# Revit family: Soap_Dispenser-Gamco-Vertical_Tank_Type-G-16AP
name_source: partatom
category: Specialty Equipment
revit_build: Autodesk Revit 2018 (Build: 20170223_1515(x64)
units: mm (PartAtom-declared; Revit-internal decimal feet)

## family parameters
Cut with Voids When Loaded = No
Host = Face
OmniClass Number = 23.40.20.21.34
OmniClass Title = Soap Holders, Dispensers
Part Type = Normal
Room Calculation Point = No
Round Connector Dimension = Use Diameter
Shared = Yes

## types (1)
- G-16AP
    ADA = Yes
    ADA Compliant = Yes
    Assembly Code = C1030200
    Capacity = 40-fl oz. (1.2-L) of liquid lotion soap
    Container Material = Metal-Gamco-Stainless Steel
    Default Elevation = 0"
    Description = Surface-Mounted Vertical Tank-Type Soap Dispenser with All-Purpose Valve
    Height = 8 1/4"
    Installation Type = Wall Mounted
    Length = 4 3/4"
    Manufacturer = GAMCO
    Material = Metal-Gamco-Stainless Steel
    Model = G-16AP
    Mounting Height = 44"
    Price = Prices may vary. Please consult Manufacturer Representative for most up-to-date price list.
    Product Documentation Link = http://gamcousa.com
    Product Page URL = https://gamcousa.com
    Push Button And Spout Material = Plastic-Gamco-Black
    URL = https://gamcousa.com
    Warranty Documentation Link = http://gamcousa.com
    Width = 3"

## geometry (parser evidence)
native form markers: Sweep x3
no freeform markers — native parametric forms only
